# Revit family: Chair-Lounge-Bernhardt_Design-Amri
name_source: partatom
category: Furniture
revit_build: Autodesk Revit Architecture 2013 (Build: 20130531_2115(x64)
units: mm (PartAtom-declared; Revit-internal decimal feet)

## types (2) — shared parameters
Arm Height = 1' - 7 1/2"
Base Finish = Wood - Bernhardt Design - Maple
Depth = 2' - 10"
Description = Chair
Height = 2' - 8 3/4"
Manufacturer = Bernhardt Design
Product Documentation Link = http://www.bernhardtdesign.com
Product Name = Amri
Product Page URL = http://www.bernhardtdesign.com
Rotation Note = Yes
Seat Height = 1' - 4"
URL = http://www.bernhardtdesign.com
Width = 2' - 9 1/2"

## per-type parameters (varying)
| type | Model | Stationary | Swivel | Upholstery |
| 4760 - Stationary | 4760 | Yes | No | Fabric- Bernhardt Design - White Linen |
| 4762 - Swivel | 4762 | No | Yes | Fabric - Bernhardt Design - Purple Linen |

## geometry (parser evidence)
native form markers: Blend x52, Sweep x5
no freeform markers — native parametric forms only
